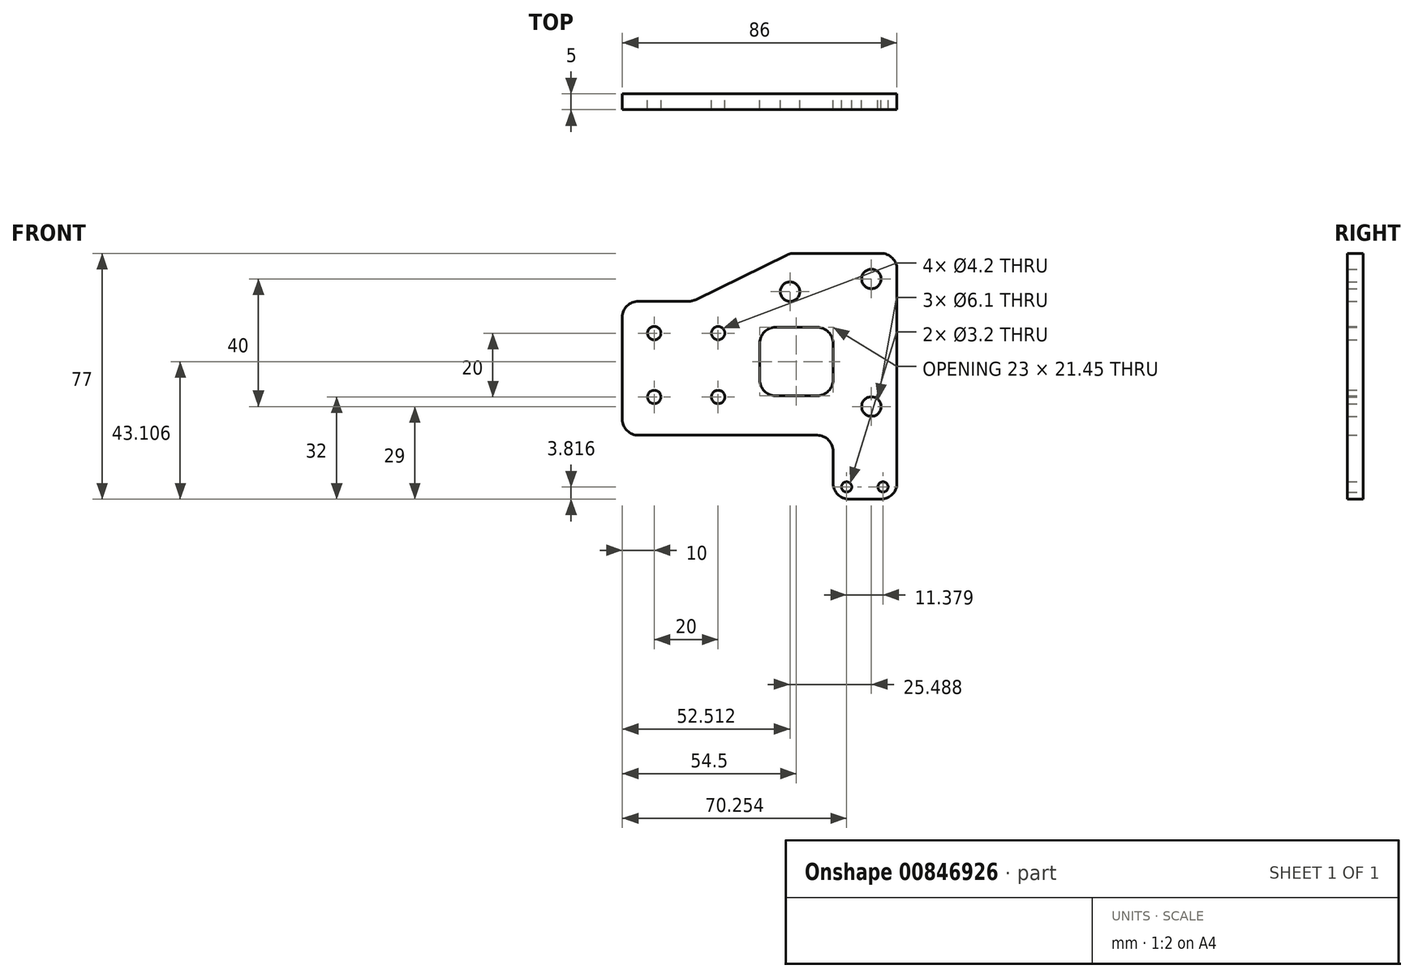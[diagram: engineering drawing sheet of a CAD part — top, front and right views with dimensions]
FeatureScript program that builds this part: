
annotation { "Feature Type Name" : "Feature", "Feature Type Description" : "" }
export const myFeature = defineFeature(function(context is Context, id is Id, definition is map)
    precondition{}
    {
        {
            var Q0;
            Q0=qCreatedBy(makeId("Front.planeOp"),FACE);
            cPlane(context, id + "F0", {"entities" : qUnion([Q0]), "cplaneType" : CPlaneType.OFFSET, "offset" : 10 * mm, "width" : 150 * mm, "height" : 150 * mm});
        }
        {
            var Q0;
            Q0=qCreatedBy(id+"F0.planeOp",FACE);
            var sketch = newSketch(context, id + "F1", { "sketchPlane" : qUnion([Q0])});
            skLineSegment(sketch, "E0", {"start": v(23, -38.5) * mm, "end": v(43, -38.5) * mm});
            skLineSegment(sketch, "E1", {"start": v(43, -38.5) * mm, "end": v(43, 38.5) * mm});
            skLineSegment(sketch, "E2", {"start": v(43, 38.5) * mm, "end": v(9.51, 38.5) * mm});
            skLineSegment(sketch, "E3", {"start": v(9.51, 38.5) * mm, "end": v(-21, 23.5) * mm});
            skLineSegment(sketch, "E4", {"start": v(-21, 23.5) * mm, "end": v(-43, 23.5) * mm});
            skLineSegment(sketch, "E5", {"start": v(-43, 23.5) * mm, "end": v(-43, -18.5) * mm});
            skCircle(sketch, "E6", {"center": v(-33, 13.5) * mm, "radius": 2.1 * mm});
            skCircle(sketch, "E7", {"center": v(-33, -6.5) * mm, "radius": 2.1 * mm});
            skCircle(sketch, "E8", {"center": v(-13, 13.5) * mm, "radius": 2.1 * mm});
            skCircle(sketch, "E9", {"center": v(-13, -6.5) * mm, "radius": 2.1 * mm});
            skCircle(sketch, "E10", {"center": v(35, 30.5) * mm, "radius": 3.05 * mm});
            skCircle(sketch, "E11", {"center": v(35, -9.5) * mm, "radius": 3.05 * mm});
            skCircle(sketch, "E12", {"center": v(9.51, 26.5) * mm, "radius": 3.05 * mm});
            skLineSegment(sketch, "E13.bottom", {"start": v(-43, -18.5) * mm, "end": v(23, -18.5) * mm});
            skLineSegment(sketch, "E13.right", {"start": v(23, -18.5) * mm, "end": v(23, -38.5) * mm});
            skLineSegment(sketch, "E14.bottom", {"start": v(0, 15.33) * mm, "end": v(23, 15.33) * mm});
            skLineSegment(sketch, "E14.top", {"start": v(0, -6.12) * mm, "end": v(23, -6.12) * mm});
            skLineSegment(sketch, "E14.left", {"start": v(0, 15.33) * mm, "end": v(0, -6.12) * mm});
            skLineSegment(sketch, "E14.right", {"start": v(23, 15.33) * mm, "end": v(23, -6.12) * mm});
            skPoint(sketch, "E15.orphan", {"position": v(-43, -38.5) * mm});
            skCircle(sketch, "E16", {"center": v(27.25, -34.68) * mm, "radius": 1.6 * mm});
            skCircle(sketch, "E17", {"center": v(38.63, -34.68) * mm, "radius": 1.6 * mm});
            skSolve(sketch);
        }
        {
            var Q0;
            Q0 = qSketchRegion(id + "F1", true);
            extrude(context, id + "F2", {"entities" : qUnion([Q0]), "depth" : 5 * mm, "offsetDistance" : 25 * mm});
        }
        {
            var Q0;
            Q0=makeQuery(id+"F2.opExtrude","SWEPT_EDGE",EDGE,{"disambiguationData":[OSD([sQuery(id+"F1.wireOp",EDGE,"E5"),sQuery(id+"F1.wireOp",EDGE,"E13.bottom")])]});
            var Q1;
            Q1=makeQuery(id+"F2.opExtrude","SWEPT_EDGE",EDGE,{"disambiguationData":[OSD([sQuery(id+"F1.wireOp",EDGE,"E4"),sQuery(id+"F1.wireOp",EDGE,"E5")])]});
            var Q2;
            Q2=makeQuery(id+"F2.opExtrude","SWEPT_EDGE",EDGE,{"disambiguationData":[OSD([sQuery(id+"F1.wireOp",EDGE,"E14.top"),sQuery(id+"F1.wireOp",EDGE,"E14.left")])]});
            var Q3;
            Q3=makeQuery(id+"F2.opExtrude","SWEPT_EDGE",EDGE,{"disambiguationData":[OSD([sQuery(id+"F1.wireOp",EDGE,"E14.bottom"),sQuery(id+"F1.wireOp",EDGE,"E14.left")])]});
            var Q4;
            Q4=makeQuery(id+"F2.opExtrude","SWEPT_EDGE",EDGE,{"disambiguationData":[OSD([sQuery(id+"F1.wireOp",EDGE,"E14.bottom"),sQuery(id+"F1.wireOp",EDGE,"E14.right")])]});
            var Q5;
            Q5=makeQuery(id+"F2.opExtrude","SWEPT_EDGE",EDGE,{"disambiguationData":[OSD([sQuery(id+"F1.wireOp",EDGE,"E14.top"),sQuery(id+"F1.wireOp",EDGE,"E14.right")])]});
            var Q6;
            Q6=makeQuery(id+"F2.opExtrude","SWEPT_EDGE",EDGE,{"disambiguationData":[OSD([sQuery(id+"F1.wireOp",EDGE,"E13.bottom"),sQuery(id+"F1.wireOp",EDGE,"E13.right")])]});
            var Q7;
            Q7=makeQuery(id+"F2.opExtrude","SWEPT_EDGE",EDGE,{"disambiguationData":[OSD([sQuery(id+"F1.wireOp",EDGE,"E0"),sQuery(id+"F1.wireOp",EDGE,"E13.right")])]});
            var Q8;
            Q8=makeQuery(id+"F2.opExtrude","SWEPT_EDGE",EDGE,{"disambiguationData":[OSD([sQuery(id+"F1.wireOp",EDGE,"E0"),sQuery(id+"F1.wireOp",EDGE,"E1")])]});
            var Q9;
            Q9=makeQuery(id+"F2.opExtrude","SWEPT_EDGE",EDGE,{"disambiguationData":[OSD([sQuery(id+"F1.wireOp",EDGE,"E1"),sQuery(id+"F1.wireOp",EDGE,"E2")])]});
            var Q10;
            Q10=makeQuery(id+"F2.opExtrude","SWEPT_EDGE",EDGE,{"disambiguationData":[OSD([sQuery(id+"F1.wireOp",EDGE,"E3"),sQuery(id+"F1.wireOp",EDGE,"E4")])]});
            var Q11;
            Q11=makeQuery(id+"F2.opExtrude","SWEPT_EDGE",EDGE,{"disambiguationData":[OSD([sQuery(id+"F1.wireOp",EDGE,"E2"),sQuery(id+"F1.wireOp",EDGE,"E3")])]});
            fillet(context, id + "F3", {"entities" : qUnion([Q0, Q1, Q2, Q3, Q4, Q5, Q6, Q7, Q8, Q9, Q10, Q11]), "radius" : 5 * mm, "tangentPropagation" : true, "allowEdgeOverflow" : false});
        }
    });
